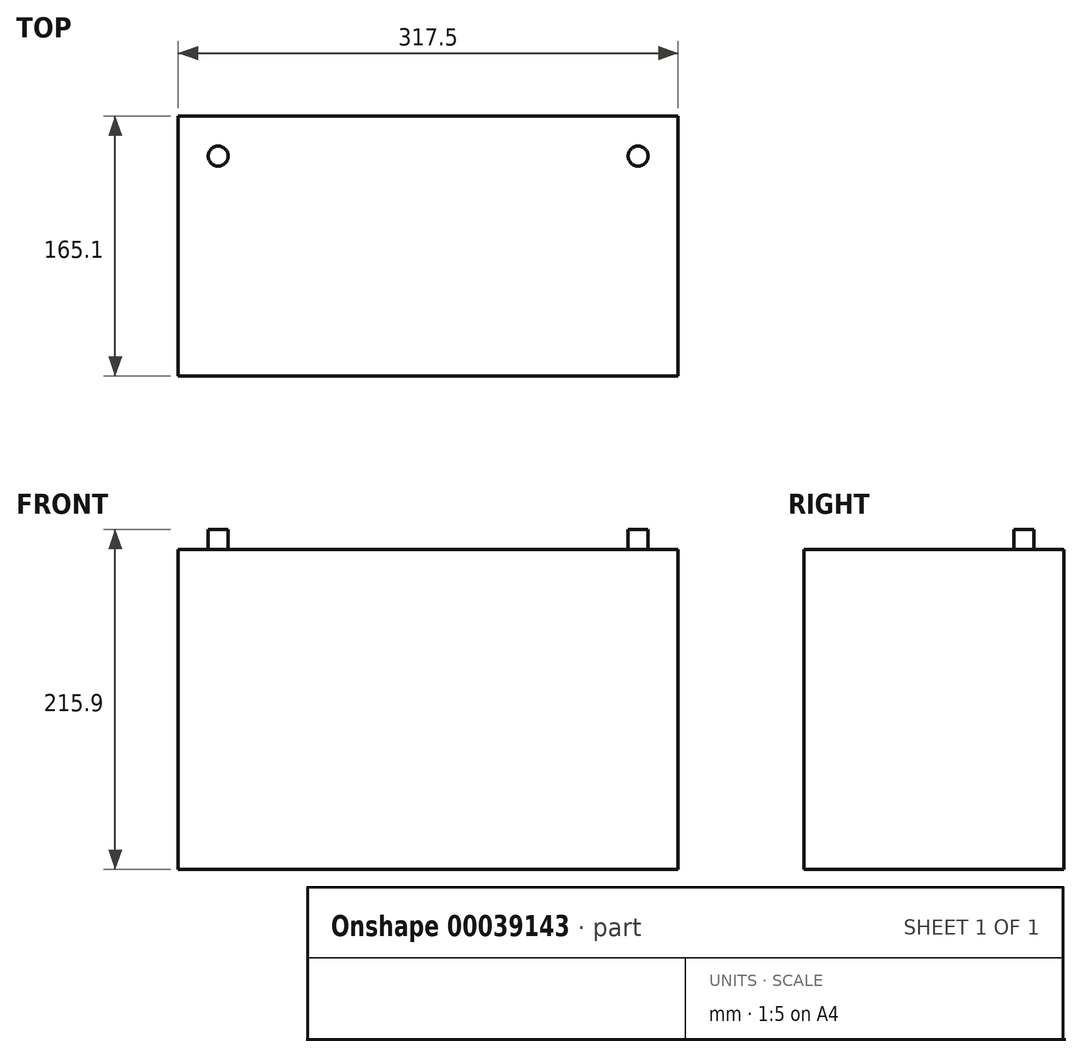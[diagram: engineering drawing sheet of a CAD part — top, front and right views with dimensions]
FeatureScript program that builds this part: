
annotation { "Feature Type Name" : "Feature", "Feature Type Description" : "" }
export const myFeature = defineFeature(function(context is Context, id is Id, definition is map)
    precondition{}
    {
        {
            var Q0;
            Q0=qCreatedBy(makeId("Top.planeOp"),FACE);
            var sketch = newSketch(context, id + "F0", { "sketchPlane" : qUnion([Q0])});
            skLineSegment(sketch, "E0.rect.bottom", {"start": v(-158.75, 82.55) * mm, "end": v(158.75, 82.55) * mm});
            skLineSegment(sketch, "E0.rect.top", {"start": v(-158.75, -82.55) * mm, "end": v(158.75, -82.55) * mm});
            skLineSegment(sketch, "E0.rect.left", {"start": v(-158.75, 82.55) * mm, "end": v(-158.75, -82.55) * mm});
            skLineSegment(sketch, "E0.rect.right", {"start": v(158.75, 82.55) * mm, "end": v(158.75, -82.55) * mm});
            skPoint(sketch, "E0.rect.middle", {"position": v(0, 0) * mm});
            skSolve(sketch);
        }
        {
            var Q0;
            Q0 = qSketchRegion(id + "F0", true);
            extrude(context, id + "F1", {"entities" : qUnion([Q0]), "endBound" : BoundingType.SYMMETRIC, "depth" : 203.2 * mm});
        }
        {
            var Q0;
            Q0=makeQuery(id+"F1.opExtrude","CAP_FACE",FACE,{"disambiguationData":[OSD([sQuery(id+"F0.wireOp",EDGE,"E0.rect.bottom"),sQuery(id+"F0.wireOp",EDGE,"E0.rect.top"),sQuery(id+"F0.wireOp",EDGE,"E0.rect.left"),sQuery(id+"F0.wireOp",EDGE,"E0.rect.right")])],"isStart":false});
            var sketch = newSketch(context, id + "F2", { "sketchPlane" : qUnion([Q0])});
            skCircle(sketch, "E1", {"center": v(-133.35, 57.15) * mm, "radius": 6.35 * mm});
            skLineSegment(sketch, "E2", {"start": v(0, -82.55) * mm, "end": v(0, 82.55) * mm, "construction": true});
            skCircle(sketch, "E3.MirrorC", {"center": v(133.35, 57.15) * mm, "radius": 6.35 * mm});
            skSolve(sketch);
        }
        {
            var Q0;
            Q0 = qSketchRegion(id + "F2", true);
            extrude(context, id + "F3", {"entities" : qUnion([Q0]), "operationType" : NewBodyOperationType.ADD, "depth" : 12.7 * mm});
        }
    });
